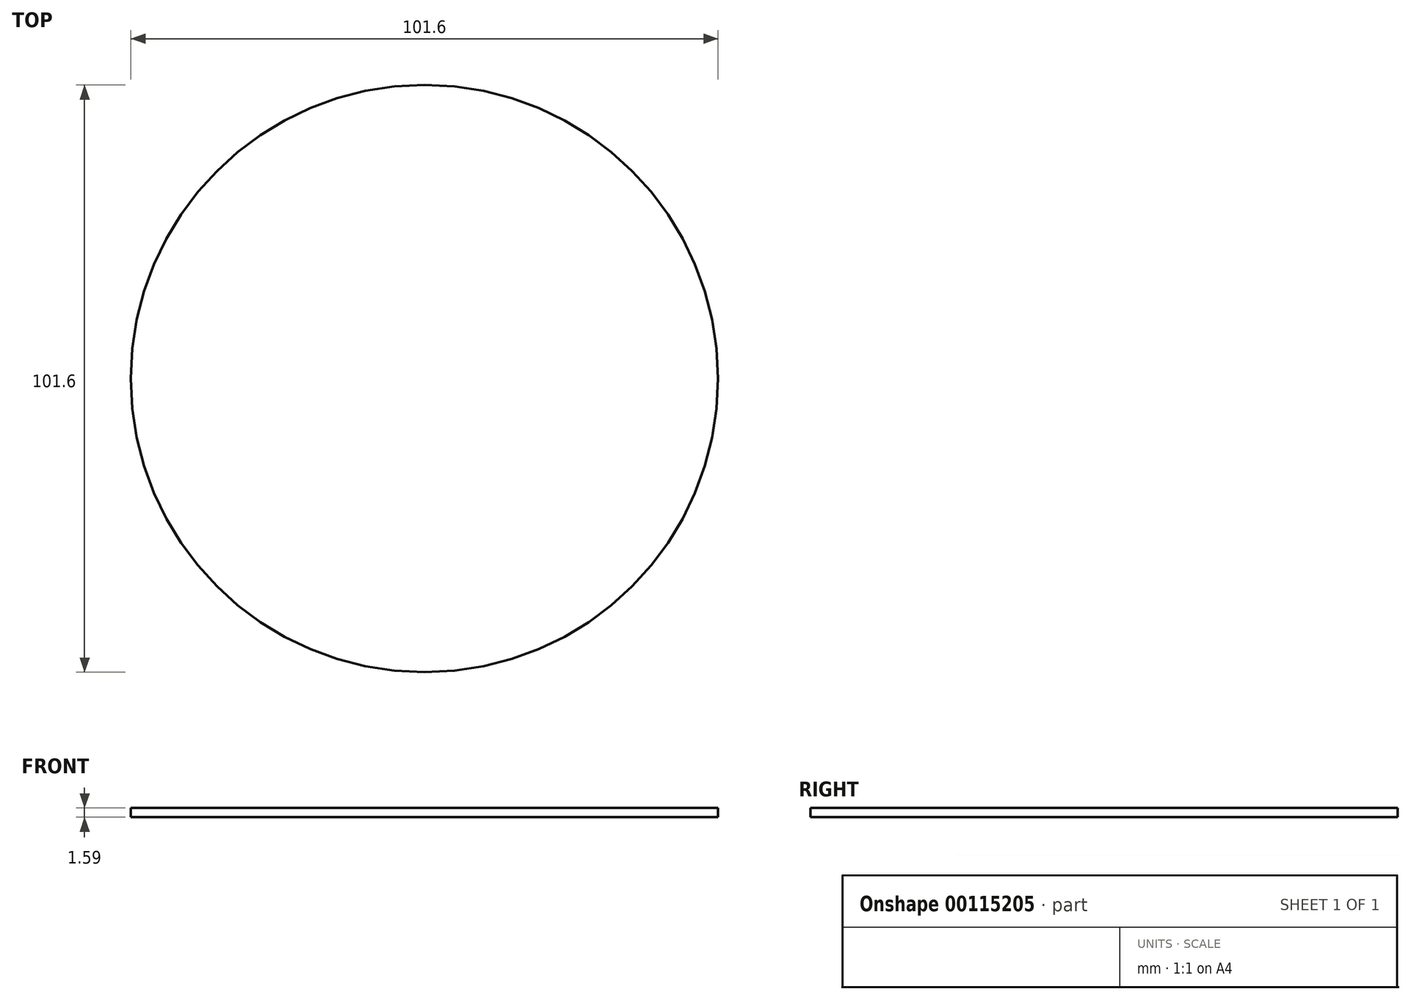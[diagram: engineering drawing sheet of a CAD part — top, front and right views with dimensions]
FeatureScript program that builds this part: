
annotation { "Feature Type Name" : "Feature", "Feature Type Description" : "" }
export const myFeature = defineFeature(function(context is Context, id is Id, definition is map)
    precondition{}
    {
        {
            var Q0;
            Q0=qCreatedBy(makeId("Top.planeOp"),FACE);
            var sketch = newSketch(context, id + "F0", { "sketchPlane" : qUnion([Q0])});
            skCircle(sketch, "E0", {"center": v(0, 0) * mm, "radius": 50.8 * mm});
            skSolve(sketch);
        }
        {
            var Q0;
            Q0=makeQuery(id+"F0.imprint","IMPRINT",FACE,{"disambiguationData":[TD([[makeQuery(id+"F0.imprint","IMPRINT",EDGE,{"derivedFrom":sQuery(id+"F0.wireOp",EDGE,"E0")}),1.0]])]});
            extrude(context, id + "F1", {"entities" : qUnion([Q0]), "depth" : 1.59 * mm});
        }
    });
